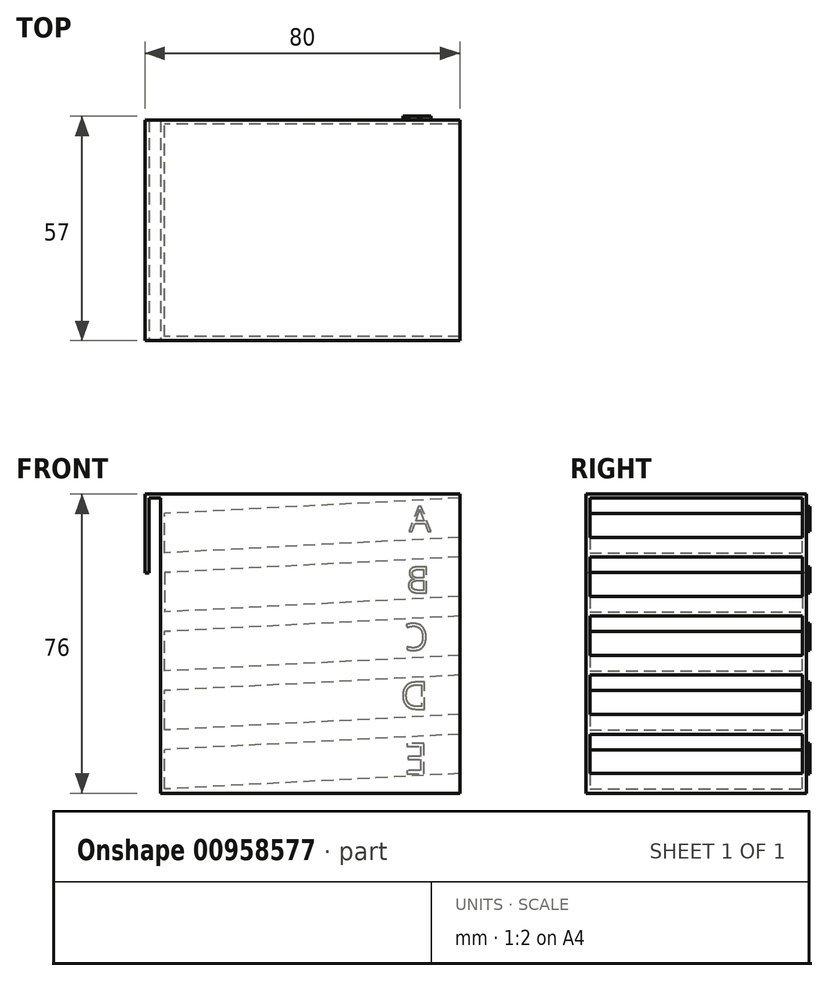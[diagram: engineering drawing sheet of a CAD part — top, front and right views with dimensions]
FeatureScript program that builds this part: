
annotation { "Feature Type Name" : "Feature", "Feature Type Description" : "" }
export const myFeature = defineFeature(function(context is Context, id is Id, definition is map)
    precondition{}
    {
        {
            var Q0;
            Q0=qCreatedBy(makeId("Front.planeOp"),FACE);
            var sketch = newSketch(context, id + "F0", { "sketchPlane" : qUnion([Q0])});
            skLineSegment(sketch, "E0.bottom", {"start": v(38, -38) * mm, "end": v(-38, -38) * mm});
            skLineSegment(sketch, "E0.top", {"start": v(38, 38) * mm, "end": v(-38, 38) * mm});
            skLineSegment(sketch, "E0.left", {"start": v(38, -38) * mm, "end": v(38, 38) * mm});
            skLineSegment(sketch, "E0.right", {"start": v(-38, -38) * mm, "end": v(-38, 38) * mm});
            skPoint(sketch, "E0.middle", {"position": v(0, 0) * mm});
            skSolve(sketch);
        }
        {
            var Q0;
            Q0=makeQuery(id+"F0.imprint","IMPRINT",FACE,{"disambiguationData":[TD([[makeQuery(id+"F0.imprint","IMPRINT",EDGE,{"derivedFrom":sQuery(id+"F0.wireOp",EDGE,"E0.bottom")}),-1.0]])]});
            extrude(context, id + "F1", {"entities" : qUnion([Q0]), "endBound" : BoundingType.SYMMETRIC, "oppositeDirection" : true, "depth" : 56 * mm, "offsetDistance" : 25 * mm});
        }
        {
            var Q0;
            Q0=makeQuery(id+"F1.opExtrude","SWEPT_FACE",FACE,{"disambiguationData":[OSD([sQuery(id+"F0.wireOp",EDGE,"E0.left")])]});
            var sketch = newSketch(context, id + "F2", { "sketchPlane" : qUnion([Q0])});
            skPoint(sketch, "E1", {"position": v(-28, 38) * mm});
            skPoint(sketch, "E2", {"position": v(-28, 37) * mm});
            skPoint(sketch, "E3", {"position": v(-27, 37) * mm});
            skLineSegment(sketch, "E4.bottom", {"start": v(-27, 37) * mm, "end": v(27, 37) * mm});
            skLineSegment(sketch, "E4.top", {"start": v(-27, 27) * mm, "end": v(27, 27) * mm});
            skLineSegment(sketch, "E4.left", {"start": v(-27, 37) * mm, "end": v(-27, 27) * mm});
            skLineSegment(sketch, "E4.right", {"start": v(27, 37) * mm, "end": v(27, 27) * mm});
            skPoint(sketch, "E5", {"position": v(-27, 27) * mm});
            skPoint(sketch, "E6", {"position": v(-27, 22) * mm});
            skLineSegment(sketch, "E7.bottom", {"start": v(-27, 22) * mm, "end": v(27, 22) * mm});
            skLineSegment(sketch, "E7.top", {"start": v(-27, 12) * mm, "end": v(27, 12) * mm});
            skLineSegment(sketch, "E7.left", {"start": v(-27, 22) * mm, "end": v(-27, 12) * mm});
            skLineSegment(sketch, "E7.right", {"start": v(27, 22) * mm, "end": v(27, 12) * mm});
            skPoint(sketch, "E8", {"position": v(-27, 7) * mm});
            skLineSegment(sketch, "E9.bottom", {"start": v(-27, 7) * mm, "end": v(27, 7) * mm});
            skLineSegment(sketch, "E9.top", {"start": v(-27, -3) * mm, "end": v(27, -3) * mm});
            skLineSegment(sketch, "E9.left", {"start": v(-27, 7) * mm, "end": v(-27, -3) * mm});
            skLineSegment(sketch, "E9.right", {"start": v(27, 7) * mm, "end": v(27, -3) * mm});
            skPoint(sketch, "E10", {"position": v(-27, -8) * mm});
            skLineSegment(sketch, "E11.bottom", {"start": v(-27, -8) * mm, "end": v(27, -8) * mm});
            skLineSegment(sketch, "E11.top", {"start": v(-27, -18) * mm, "end": v(27, -18) * mm});
            skLineSegment(sketch, "E11.left", {"start": v(-27, -8) * mm, "end": v(-27, -18) * mm});
            skLineSegment(sketch, "E11.right", {"start": v(27, -8) * mm, "end": v(27, -18) * mm});
            skPoint(sketch, "E12", {"position": v(-27, -23) * mm});
            skLineSegment(sketch, "E13.bottom", {"start": v(-27, -23) * mm, "end": v(27, -23) * mm});
            skLineSegment(sketch, "E13.top", {"start": v(-27, -33) * mm, "end": v(27, -33) * mm});
            skLineSegment(sketch, "E13.left", {"start": v(-27, -23) * mm, "end": v(-27, -33) * mm});
            skLineSegment(sketch, "E13.right", {"start": v(27, -23) * mm, "end": v(27, -33) * mm});
            skSolve(sketch);
        }
        {
            var Q0;
            Q0=makeQuery(id+"F1.opExtrude","CAP_FACE",FACE,{"disambiguationData":[OSD([sQuery(id+"F0.wireOp",EDGE,"E0.bottom"),sQuery(id+"F0.wireOp",EDGE,"E0.top"),sQuery(id+"F0.wireOp",EDGE,"E0.left"),sQuery(id+"F0.wireOp",EDGE,"E0.right")])],"isStart":true});
            var sketch = newSketch(context, id + "F3", { "sketchPlane" : qUnion([Q0])});
            skPoint(sketch, "E14", {"position": v(38, 22) * mm});
            skPoint(sketch, "E15", {"position": v(38, 7) * mm});
            skPoint(sketch, "E16", {"position": v(38, -8) * mm});
            skPoint(sketch, "E17", {"position": v(38, -23) * mm});
            skPoint(sketch, "E18", {"position": v(38, 37) * mm});
            skLineSegment(sketch, "E19", {"start": v(-38, 33.02) * mm, "end": v(-10.2, 33.02) * mm, "construction": true});
            skLineSegment(sketch, "E20", {"start": v(38, 37) * mm, "end": v(-38, 33.02) * mm});
            skLineSegment(sketch, "E21", {"start": v(38, 22) * mm, "end": v(-38, 18.02) * mm});
            skLineSegment(sketch, "E22", {"start": v(-38, 18.02) * mm, "end": v(-8.95, 18.02) * mm, "construction": true});
            skLineSegment(sketch, "E23", {"start": v(38, -23) * mm, "end": v(-38, -26.98) * mm});
            skLineSegment(sketch, "E24", {"start": v(-38, -26.98) * mm, "end": v(-9.06, -26.98) * mm, "construction": true});
            skLineSegment(sketch, "E25", {"start": v(38, 7) * mm, "end": v(-38, 3.02) * mm});
            skLineSegment(sketch, "E26", {"start": v(-38, 3.02) * mm, "end": v(-5.53, 3.02) * mm, "construction": true});
            skLineSegment(sketch, "E27", {"start": v(38, -8) * mm, "end": v(-38, -11.98) * mm});
            skLineSegment(sketch, "E28", {"start": v(-38, -11.98) * mm, "end": v(-6.01, -11.98) * mm});
            skSolve(sketch);
        }
        {
            var Q0;
            Q0=makeQuery(id+"F2.imprint","IMPRINT",FACE,{"disambiguationData":[TD([[makeQuery(id+"F2.imprint","IMPRINT",EDGE,{"derivedFrom":sQuery(id+"F2.wireOp",EDGE,"E4.bottom")}),-1.0]])]});
            var Q1;
            Q1=makeQuery(id+"F2.imprint","IMPRINT",FACE,{"disambiguationData":[TD([[makeQuery(id+"F2.imprint","IMPRINT",EDGE,{"derivedFrom":sQuery(id+"F2.wireOp",EDGE,"E7.bottom")}),-1.0]])]});
            var Q2;
            Q2=makeQuery(id+"F2.imprint","IMPRINT",FACE,{"disambiguationData":[TD([[makeQuery(id+"F2.imprint","IMPRINT",EDGE,{"derivedFrom":sQuery(id+"F2.wireOp",EDGE,"E9.bottom")}),-1.0]])]});
            var Q3;
            Q3=makeQuery(id+"F2.imprint","IMPRINT",FACE,{"disambiguationData":[TD([[makeQuery(id+"F2.imprint","IMPRINT",EDGE,{"derivedFrom":sQuery(id+"F2.wireOp",EDGE,"E11.bottom")}),-1.0]])]});
            var Q4;
            Q4=makeQuery(id+"F2.imprint","IMPRINT",FACE,{"disambiguationData":[TD([[makeQuery(id+"F2.imprint","IMPRINT",EDGE,{"derivedFrom":sQuery(id+"F2.wireOp",EDGE,"E13.bottom")}),-1.0]])]});
            var Q5;
            Q5=sQuery(id+"F3.wireOp",EDGE,"E20");
            sweep(context, id + "F4", {"operationType" : NewBodyOperationType.REMOVE, "profiles" : qUnion([Q0, Q1, Q2, Q3, Q4]), "path" : qUnion([Q5])});
        }
        {
            var Q0;
            Q0=makeQuery(id+"F1.opExtrude","SWEPT_FACE",FACE,{"disambiguationData":[OSD([sQuery(id+"F0.wireOp",EDGE,"E0.right")])]});
            var sketch = newSketch(context, id + "F5", { "sketchPlane" : qUnion([Q0])});
            skLineSegment(sketch, "E29.bottom", {"start": v(-28, 38) * mm, "end": v(28, 38) * mm});
            skLineSegment(sketch, "E29.top", {"start": v(-28, -38) * mm, "end": v(28, -38) * mm});
            skLineSegment(sketch, "E29.left", {"start": v(-28, 38) * mm, "end": v(-28, -38) * mm});
            skLineSegment(sketch, "E29.right", {"start": v(28, 38) * mm, "end": v(28, -38) * mm});
            skSolve(sketch);
        }
        {
            var Q0;
            Q0 = qSketchRegion(id + "F5", true);
            extrude(context, id + "F6", {"entities" : qUnion([Q0]), "operationType" : NewBodyOperationType.ADD, "oppositeDirection" : true, "depth" : 1 * mm, "offsetDistance" : 25 * mm});
        }
        {
            var Q0;
            Q0=makeQuery(id+"F1.opExtrude","CAP_FACE",FACE,{"disambiguationData":[OSD([sQuery(id+"F0.wireOp",EDGE,"E0.bottom"),sQuery(id+"F0.wireOp",EDGE,"E0.top"),sQuery(id+"F0.wireOp",EDGE,"E0.left"),sQuery(id+"F0.wireOp",EDGE,"E0.right")])],"isStart":true});
            var sketch = newSketch(context, id + "F7", { "sketchPlane" : qUnion([Q0])});
            skLineSegment(sketch, "E30", {"start": v(-38, 38) * mm, "end": v(-42, 38) * mm});
            skLineSegment(sketch, "E31", {"start": v(-42, 38) * mm, "end": v(-42, 18) * mm});
            skLineSegment(sketch, "E32", {"start": v(-42, 18) * mm, "end": v(-41, 18) * mm});
            skLineSegment(sketch, "E33", {"start": v(-41, 18) * mm, "end": v(-41, 37) * mm});
            skLineSegment(sketch, "E34", {"start": v(-41, 37) * mm, "end": v(-38, 37) * mm});
            skSolve(sketch);
        }
        {
            var Q0;
            {var subQ0=sQuery(id+"F7.wireOp",EDGE,"E30");Q0=makeQuery(id+"F7.imprint","IMPRINT",FACE,{"disambiguationData":[TD([[makeQuery(id+"F7.imprint","IMPRINT",EDGE,{"derivedFrom":subQ0}),1.0]])]});}
            extrude(context, id + "F8", {"entities" : qUnion([Q0]), "operationType" : NewBodyOperationType.ADD, "oppositeDirection" : true, "depth" : 56 * mm, "offsetDistance" : 25 * mm});
        }
        {
            var Q0;
            {var subQ0=sQuery(id+"F0.wireOp",EDGE,"E0.right");Q0=makeQuery(id+"F8.boolean.opBoolean","MERGE",FACE,{"derivedFrom":[makeQuery(id+"F1.opExtrude","CAP_FACE",FACE,{"disambiguationData":[OSD([sQuery(id+"F0.wireOp",EDGE,"E0.bottom"),sQuery(id+"F0.wireOp",EDGE,"E0.top"),sQuery(id+"F0.wireOp",EDGE,"E0.left"),subQ0])],"isStart":false}),makeQuery(id+"F8.opExtrude","CAP_FACE",FACE,{"disambiguationData":[OSD([subQ0,sQuery(id+"F7.wireOp",EDGE,"E30"),sQuery(id+"F7.wireOp",EDGE,"E31"),sQuery(id+"F7.wireOp",EDGE,"E32"),sQuery(id+"F7.wireOp",EDGE,"E33"),sQuery(id+"F7.wireOp",EDGE,"E34")])],"isStart":false})]});}
            var sketch = newSketch(context, id + "F9", { "sketchPlane" : qUnion([Q0])});
            skText(sketch, "E35", { "text": "A", "fontName": "OpenSans-Regular.ttf"});
            skText(sketch, "E36", { "text": "B", "fontName": "OpenSans-Regular.ttf"});
            skText(sketch, "E37", { "text": "C", "fontName": "OpenSans-Regular.ttf"});
            skText(sketch, "E38", { "text": "D", "fontName": "OpenSans-Regular.ttf"});
            skText(sketch, "E39", { "text": "E", "fontName": "OpenSans-Regular.ttf"});
            const initialGuessF9  = {"E35": [-0.03067, 0.02852, 1, 0, 0.00643], "E36": [-0.03044, 0.01292, 1, 0, 0.00667], "E37": [-0.02997, -0.00164, 1, 0, 0.00676], "E38": [-0.02997, -0.01666, 1, 0, 0.00695], "E39": [-0.02997, -0.03303, 1, 0, 0.0078]};
            skSetInitialGuess(sketch, initialGuessF9);
            skSolve(sketch);
        }
        {
            var Q0;
            Q0 = qSketchRegion(id + "F9", true);
            extrude(context, id + "F10", {"entities" : qUnion([Q0]), "operationType" : NewBodyOperationType.ADD, "depth" : 1 * mm, "offsetDistance" : 25 * mm});
        }
    });
